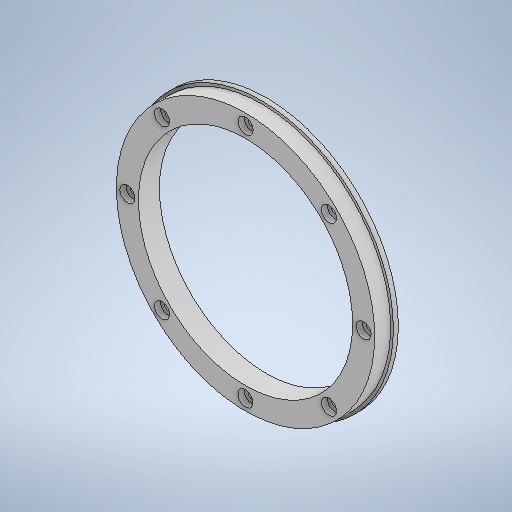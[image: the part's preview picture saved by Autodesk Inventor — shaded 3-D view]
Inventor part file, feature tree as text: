
AUTODESK INVENTOR PART (.ipt)
format: ipt  version: 2025 (Build 290162010, 162A)  size: 329,216 bytes
history: native  units: mm
features: extrude x4, sketch x4, pattern_circular x1, projected_geometry x1
ambient origin geometry x8: Origin, YZ Plane, XZ Plane, XY Plane, X Axis, Y Axis, Z Axis, Center Point
bodies: Solid1 (feature_tree)
feature tree (10):
  extrude  "Extrusion1"  Depth=389.0mm
  extrude  "Extrusion2"  Depth=38.0mm
  extrude  "Extrusion3"  Depth=80.0mm TaperAngle=360.0deg
  pattern_circular  "Circular Pattern1"  [2 undecoded]
  extrude  "Extrusion4"  Depth=9.0mm
  sketch  "Sketch1"  dims[d0=40.0mm d1=389.0mm]
  sketch  "Sketch2"  dims[d2=38.0mm d3=0.0mm d4=12.5mm]
  projected_geometry  "Projected Loop1"
  sketch  "Sketch3"  dims[d5=0.0mm d6=0.0mm d7=80.0mm d8=360.0deg]
  sketch  "Sketch4"  dims[d10=27.5mm d11=11.0mm d12=0.0mm d13=5.0mm d14=9.0mm d15=0.0mm]
note: 2 required parameter values undecoded (feature->parameter linkage not recoverable at this tier; creation-order binding heuristic only, values carry confidence <= 0.55)
